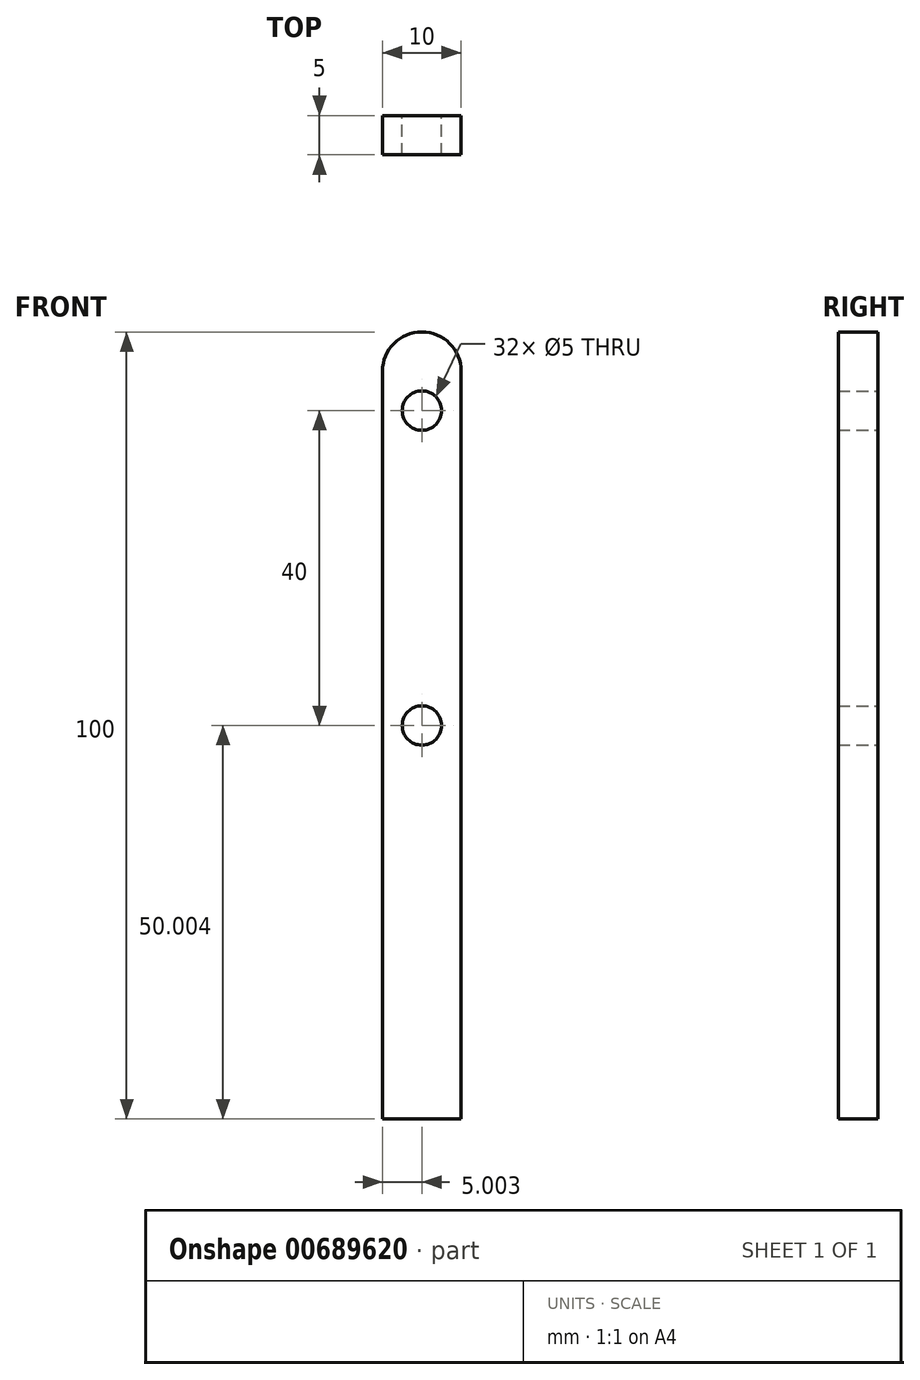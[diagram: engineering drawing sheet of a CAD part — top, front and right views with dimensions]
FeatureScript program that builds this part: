
annotation { "Feature Type Name" : "Feature", "Feature Type Description" : "" }
export const myFeature = defineFeature(function(context is Context, id is Id, definition is map)
    precondition{}
    {
        {
            var Q0;
            Q0=qCreatedBy(makeId("Front.planeOp"),FACE);
            var sketch = newSketch(context, id + "F0", { "sketchPlane" : qUnion([Q0])});
            skLineSegment(sketch, "E0.bottom", {"start": v(-48.9, 97.71) * mm, "end": v(-38.9, 97.71) * mm});
            skLineSegment(sketch, "E0.top", {"start": v(-48.9, -2.29) * mm, "end": v(-38.9, -2.29) * mm});
            skLineSegment(sketch, "E0.left", {"start": v(-48.9, 97.71) * mm, "end": v(-48.9, -2.29) * mm});
            skLineSegment(sketch, "E0.right", {"start": v(-38.9, 97.71) * mm, "end": v(-38.9, -2.29) * mm});
            skCircle(sketch, "E1", {"center": v(-43.9, 47.71) * mm, "radius": 2.5 * mm});
            skCircle(sketch, "E2", {"center": v(-43.9, 87.71) * mm, "radius": 2.5 * mm});
            skSolve(sketch);
        }
        {
            var Q0;
            Q0=makeQuery(id+"F0.imprint","IMPRINT",FACE,{"disambiguationData":[TD([[makeQuery(id+"F0.imprint","IMPRINT",EDGE,{"derivedFrom":sQuery(id+"F0.wireOp",EDGE,"E0.bottom")}),-1.0]])]});
            extrude(context, id + "F1", {"entities" : qUnion([Q0]), "depth" : 5 * mm, "offsetDistance" : 25 * mm});
        }
        {
            var Q0;
            Q0=makeQuery(id+"F1.opExtrude","SWEPT_EDGE",EDGE,{"disambiguationData":[OSD([sQuery(id+"F0.wireOp",EDGE,"E0.bottom"),sQuery(id+"F0.wireOp",EDGE,"E0.left")])]});
            var Q1;
            Q1=makeQuery(id+"F1.opExtrude","SWEPT_EDGE",EDGE,{"disambiguationData":[OSD([sQuery(id+"F0.wireOp",EDGE,"E0.bottom"),sQuery(id+"F0.wireOp",EDGE,"E0.right")])]});
            fillet(context, id + "F2", {"entities" : qUnion([Q0, Q1]), "radius" : 5 * mm, "tangentPropagation" : true, "allowEdgeOverflow" : false});
        }
    });
